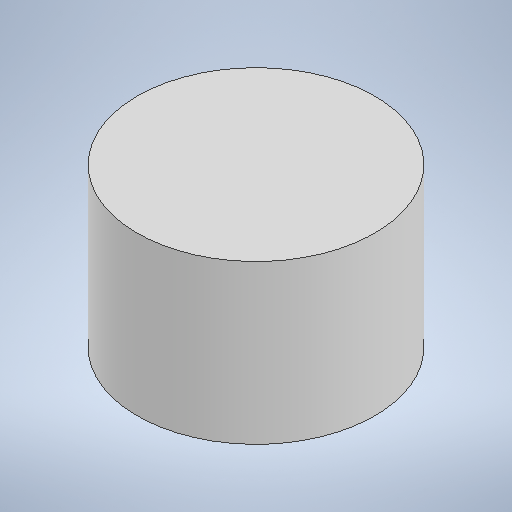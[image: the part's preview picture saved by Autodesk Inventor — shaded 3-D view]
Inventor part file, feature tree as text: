
AUTODESK INVENTOR PART (.ipt)
format: ipt  version: 2025 (Build 290162000, 162)  size: 255,488 bytes
history: native  units: in
note: dims shown in document units (in); Inventor stores cm internally (conversion verified against a paired STEP export)
features: extrude x1, sketch x1
ambient origin geometry x8: Origin, YZ Plane, XZ Plane, XY Plane, X Axis, Y Axis, Z Axis, Center Point
bodies: Solid1 (feature_tree)
feature tree (2):
  extrude  "Extrusion1"  Depth=0.1181in TaperAngle=0.0deg
  sketch  "Sketch1"  dims[d0=0.1772in d1=0.1181in d2=0.0in]
